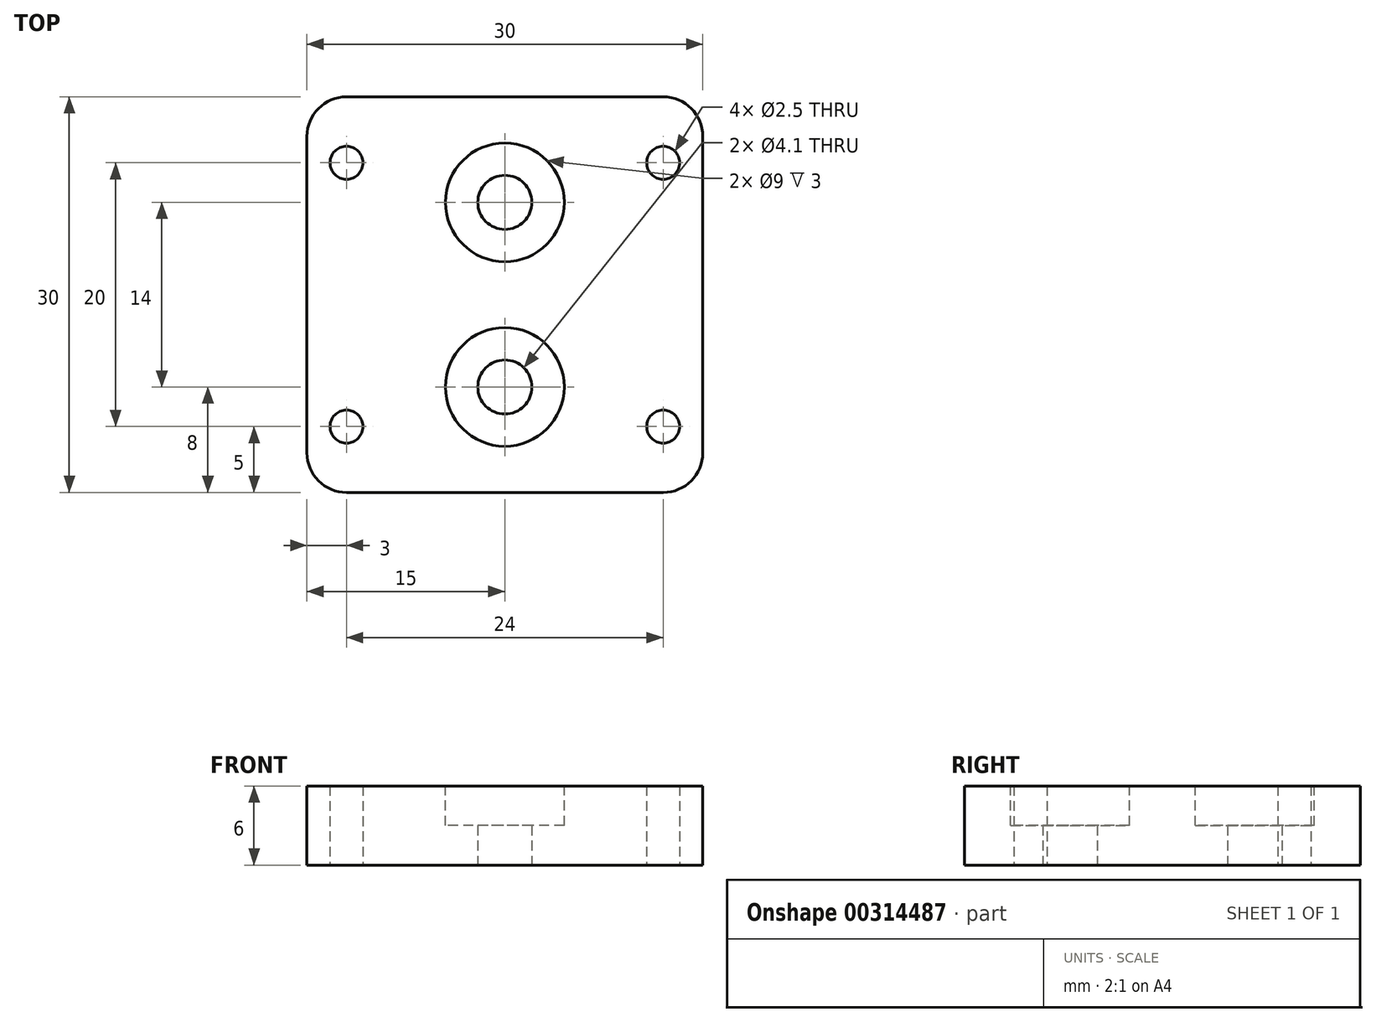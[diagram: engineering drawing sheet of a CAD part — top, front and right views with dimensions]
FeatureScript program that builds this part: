
annotation { "Feature Type Name" : "Feature", "Feature Type Description" : "" }
export const myFeature = defineFeature(function(context is Context, id is Id, definition is map)
    precondition{}
    {
        {
            var Q0;
            Q0=qCreatedBy(makeId("Top.planeOp"),FACE);
            var sketch = newSketch(context, id + "F0", { "sketchPlane" : qUnion([Q0])});
            skLineSegment(sketch, "E0.bottom", {"start": v(-15, -15) * mm, "end": v(15, -15) * mm});
            skLineSegment(sketch, "E0.top", {"start": v(-15, 15) * mm, "end": v(15, 15) * mm});
            skLineSegment(sketch, "E0.left", {"start": v(-15, -15) * mm, "end": v(-15, 15) * mm});
            skLineSegment(sketch, "E0.right", {"start": v(15, -15) * mm, "end": v(15, 15) * mm});
            skPoint(sketch, "E0.middle", {"position": v(0, 0) * mm});
            skLineSegment(sketch, "E1", {"start": v(9, 15) * mm, "end": v(9, -15) * mm, "construction": true});
            skLineSegment(sketch, "E2", {"start": v(12, 15) * mm, "end": v(12, -15) * mm, "construction": true});
            skCircle(sketch, "E3", {"center": v(12, 10) * mm, "radius": 1.25 * mm});
            skCircle(sketch, "E4", {"center": v(12, -10) * mm, "radius": 1.25 * mm});
            skCircle(sketch, "E5.MirrorC", {"center": v(-12, -10) * mm, "radius": 1.25 * mm});
            skCircle(sketch, "E6.MirrorC", {"center": v(-12, 10) * mm, "radius": 1.25 * mm});
            skCircle(sketch, "E7", {"center": v(0, 7) * mm, "radius": 2.05 * mm});
            skCircle(sketch, "E8", {"center": v(0, -7) * mm, "radius": 2.05 * mm});
            skSolve(sketch);
        }
        {
            var Q0;
            Q0=makeQuery(id+"F0.imprint","IMPRINT",FACE,{"disambiguationData":[TD([[makeQuery(id+"F0.imprint","IMPRINT",EDGE,{"derivedFrom":sQuery(id+"F0.wireOp",EDGE,"E0.bottom")}),1.0]])]});
            extrude(context, id + "F1", {"entities" : qUnion([Q0]), "depth" : 6 * mm});
        }
        {
            var Q0;
            Q0=makeQuery(id+"F1.opExtrude","CAP_FACE",FACE,{"disambiguationData":[OSD([sQuery(id+"F0.wireOp",EDGE,"E0.bottom"),sQuery(id+"F0.wireOp",EDGE,"E0.top"),sQuery(id+"F0.wireOp",EDGE,"E0.left"),sQuery(id+"F0.wireOp",EDGE,"E0.right"),sQuery(id+"F0.wireOp",EDGE,"E3"),sQuery(id+"F0.wireOp",EDGE,"E4"),sQuery(id+"F0.wireOp",EDGE,"E5.MirrorC"),sQuery(id+"F0.wireOp",EDGE,"E6.MirrorC"),sQuery(id+"F0.wireOp",EDGE,"E7"),sQuery(id+"F0.wireOp",EDGE,"E8")])],"isStart":false});
            var sketch = newSketch(context, id + "F2", { "sketchPlane" : qUnion([Q0])});
            skCircle(sketch, "E9", {"center": v(0, 7) * mm, "radius": 4.5 * mm});
            skCircle(sketch, "E10", {"center": v(0, -7) * mm, "radius": 4.5 * mm});
            skSolve(sketch);
        }
        {
            var Q0;
            Q0 = qSketchRegion(id + "F2", true);
            extrude(context, id + "F3", {"entities" : qUnion([Q0]), "operationType" : NewBodyOperationType.REMOVE, "oppositeDirection" : true, "depth" : 3 * mm});
        }
        {
            var Q0;
            Q0=makeQuery(id+"F1.opExtrude","SWEPT_EDGE",EDGE,{"disambiguationData":[OSD([sQuery(id+"F0.wireOp",EDGE,"E0.bottom"),sQuery(id+"F0.wireOp",EDGE,"E0.right")])]});
            var Q1;
            Q1=makeQuery(id+"F1.opExtrude","SWEPT_EDGE",EDGE,{"disambiguationData":[OSD([sQuery(id+"F0.wireOp",EDGE,"E0.top"),sQuery(id+"F0.wireOp",EDGE,"E0.right")])]});
            var Q2;
            Q2=makeQuery(id+"F1.opExtrude","SWEPT_EDGE",EDGE,{"disambiguationData":[OSD([sQuery(id+"F0.wireOp",EDGE,"E0.bottom"),sQuery(id+"F0.wireOp",EDGE,"E0.left")])]});
            var Q3;
            Q3=makeQuery(id+"F1.opExtrude","SWEPT_EDGE",EDGE,{"disambiguationData":[OSD([sQuery(id+"F0.wireOp",EDGE,"E0.top"),sQuery(id+"F0.wireOp",EDGE,"E0.left")])]});
            fillet(context, id + "F4", {"entities" : qUnion([Q0, Q1, Q2, Q3]), "radius" : 3 * mm, "tangentPropagation" : true, "allowEdgeOverflow" : false});
        }
    });
